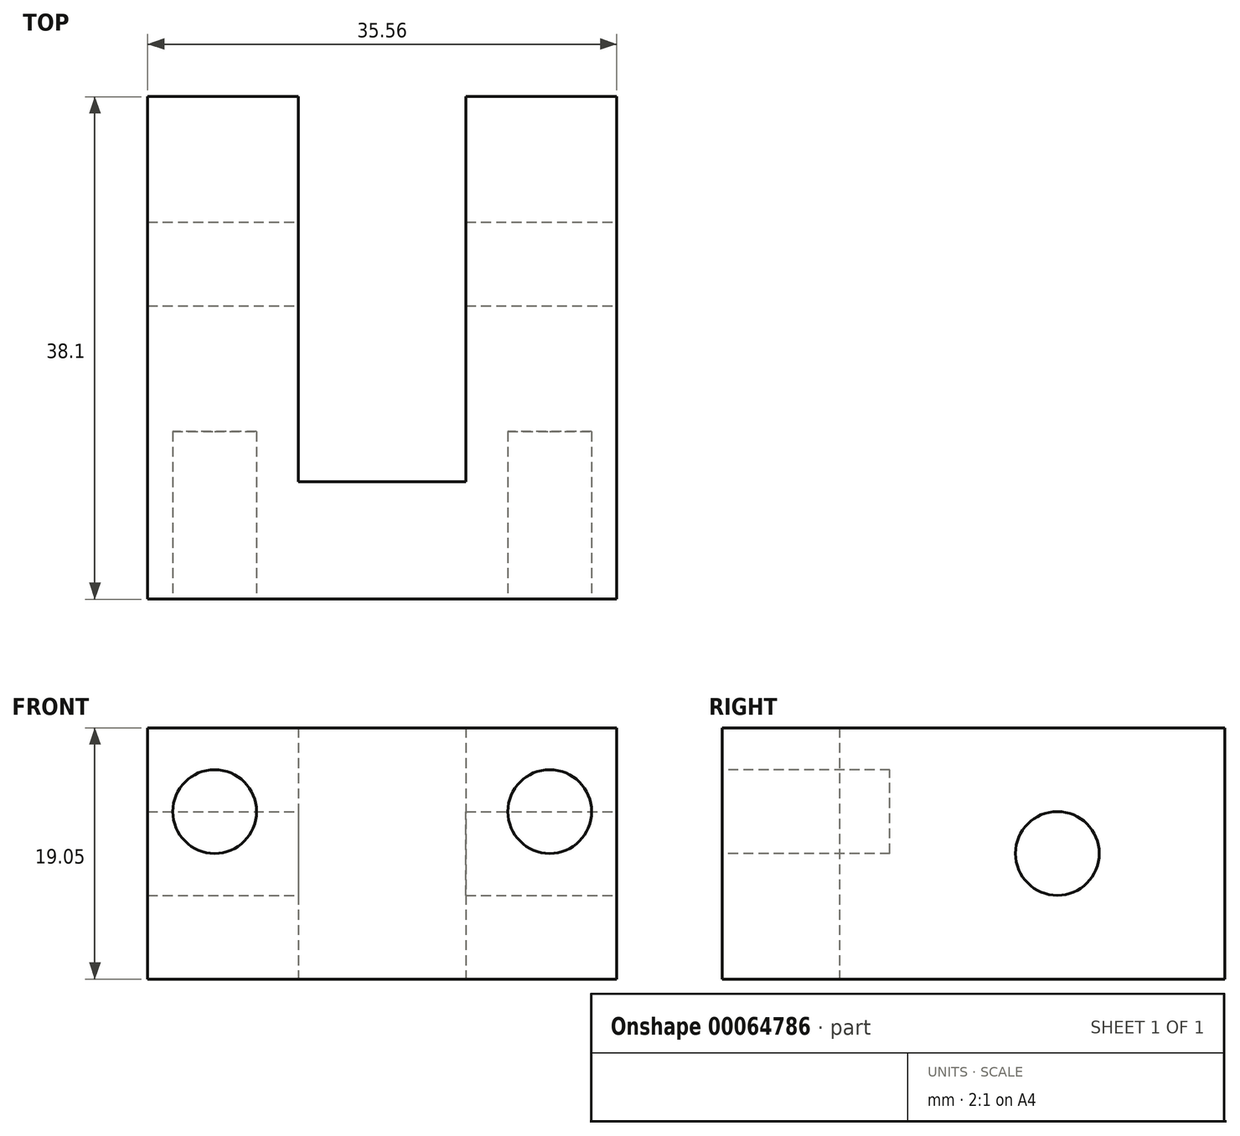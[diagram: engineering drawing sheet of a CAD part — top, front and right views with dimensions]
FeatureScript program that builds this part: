
annotation { "Feature Type Name" : "Feature", "Feature Type Description" : "" }
export const myFeature = defineFeature(function(context is Context, id is Id, definition is map)
    precondition{}
    {
        {
            var Q0;
            Q0=qCreatedBy(makeId("Top.planeOp"),FACE);
            var sketch = newSketch(context, id + "F0", { "sketchPlane" : qUnion([Q0])});
            skLineSegment(sketch, "E0", {"start": v(0, 41.82) * mm, "end": v(0, -44) * mm, "construction": true});
            skLineSegment(sketch, "E1", {"start": v(-33.93, 0) * mm, "end": v(47.72, 0) * mm, "construction": true});
            skLineSegment(sketch, "E2", {"start": v(-17.78, 0.45) * mm, "end": v(-17.78, -37.65) * mm});
            skLineSegment(sketch, "E3", {"start": v(-17.78, -37.65) * mm, "end": v(17.78, -37.65) * mm});
            skLineSegment(sketch, "E4", {"start": v(17.78, -37.65) * mm, "end": v(17.78, 0.45) * mm});
            skLineSegment(sketch, "E5", {"start": v(17.78, 0.45) * mm, "end": v(6.35, 0.45) * mm});
            skLineSegment(sketch, "E6", {"start": v(6.35, 0.45) * mm, "end": v(6.35, -28.76) * mm});
            skLineSegment(sketch, "E7", {"start": v(6.35, -28.76) * mm, "end": v(-6.35, -28.76) * mm});
            skLineSegment(sketch, "E8", {"start": v(-6.35, -28.76) * mm, "end": v(-6.35, 0.45) * mm});
            skLineSegment(sketch, "E9", {"start": v(-6.35, 0.45) * mm, "end": v(-17.78, 0.45) * mm});
            skSolve(sketch);
        }
        {
            var Q0;
            Q0=qSketchRegion(id+"F0",true);
            extrude(context, id + "F1", {"entities" : qUnion([Q0]), "depth" : 19.05 * mm});
        }
        {
            var Q0;
            Q0=makeQuery(id+"F1.opExtrude","SWEPT_FACE",FACE,{"disambiguationData":[OSD([sQuery(id+"F0.wireOp",EDGE,"E3")])]});
            var sketch = newSketch(context, id + "F2", { "sketchPlane" : qUnion([Q0])});
            skCircle(sketch, "E10", {"center": v(-12.7, 12.7) * mm, "radius": 3.18 * mm});
            skCircle(sketch, "E11", {"center": v(12.7, 12.7) * mm, "radius": 3.18 * mm});
            skSolve(sketch);
        }
        {
            var Q0;
            Q0=qSketchRegion(id+"F2",true);
            extrude(context, id + "F3", {"entities" : qUnion([Q0]), "operationType" : NewBodyOperationType.REMOVE, "oppositeDirection" : true, "depth" : 12.7 * mm});
        }
        {
            var Q0;
            Q0=makeQuery(id+"F1.opExtrude","SWEPT_FACE",FACE,{"disambiguationData":[OSD([sQuery(id+"F0.wireOp",EDGE,"E4")])]});
            var sketch = newSketch(context, id + "F4", { "sketchPlane" : qUnion([Q0])});
            skCircle(sketch, "E12", {"center": v(-12.25, 9.53) * mm, "radius": 3.17 * mm});
            skSolve(sketch);
        }
        {
            var Q0;
            Q0=qSketchRegion(id+"F4",true);
            extrude(context, id + "F5", {"entities" : qUnion([Q0]), "operationType" : NewBodyOperationType.REMOVE, "endBound" : BoundingType.THROUGH_ALL, "oppositeDirection" : true, "depth" : 25.4 * mm, "hasSecondDirection" : true, "secondDirectionOppositeDirection" : false, "secondDirectionDepth" : 25.4 * mm});
        }
    });
